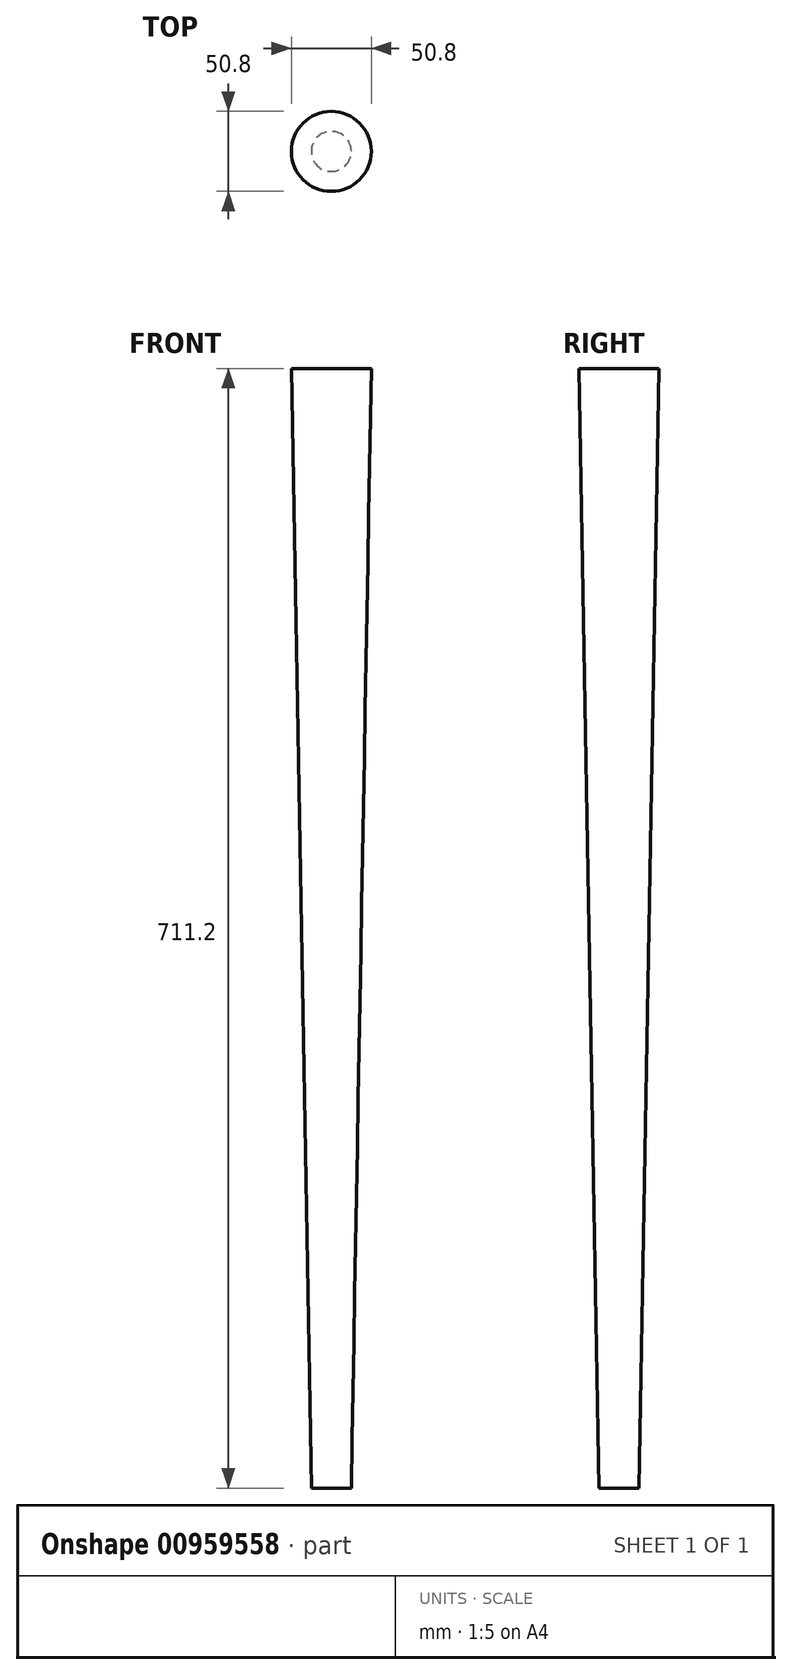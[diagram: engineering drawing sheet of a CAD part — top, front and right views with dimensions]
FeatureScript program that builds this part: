
annotation { "Feature Type Name" : "Feature", "Feature Type Description" : "" }
export const myFeature = defineFeature(function(context is Context, id is Id, definition is map)
    precondition{}
    {
        {
            var Q0;
            Q0=qCreatedBy(makeId("Top.planeOp"),FACE);
            var sketch = newSketch(context, id + "F0", { "sketchPlane" : qUnion([Q0])});
            skCircle(sketch, "E0", {"center": v(-100.73, -42.46) * mm, "radius": 12.7 * mm});
            skSolve(sketch);
        }
        {
            var Q0;
            Q0=qCreatedBy(makeId("Top.planeOp"),FACE);
            cPlane(context, id + "F1", {"entities" : qUnion([Q0]), "cplaneType" : CPlaneType.OFFSET, "offset" : 711.2 * mm, "width" : 152.4 * mm, "height" : 152.4 * mm});
        }
        {
            var Q0;
            Q0=qCreatedBy(id+"F1.planeOp",FACE);
            var sketch = newSketch(context, id + "F2", { "sketchPlane" : qUnion([Q0])});
            skPoint(sketch, "E1.0", {"position": v(-100.73, -42.46) * mm});
            skCircle(sketch, "E2", {"center": v(-100.73, -42.46) * mm, "radius": 25.4 * mm});
            skSolve(sketch);
        }
        {
            var Q0;
            Q0=makeQuery(id+"F0.imprint","IMPRINT",FACE,{"disambiguationData":[TD([[makeQuery(id+"F0.imprint","IMPRINT",EDGE,{"derivedFrom":sQuery(id+"F0.wireOp",EDGE,"E0")}),1.0]])]});
            var Q1;
            Q1=makeQuery(id+"F2.imprint","IMPRINT",FACE,{"disambiguationData":[TD([[makeQuery(id+"F2.imprint","IMPRINT",EDGE,{"derivedFrom":sQuery(id+"F2.wireOp",EDGE,"E2")}),1.0]])]});
            loft(context, id + "F3", {"sheetProfilesArray" : [{ "sheetProfileEntities" : qUnion([Q0]) }, { "sheetProfileEntities" : qUnion([Q1]) }]});
        }
    });
